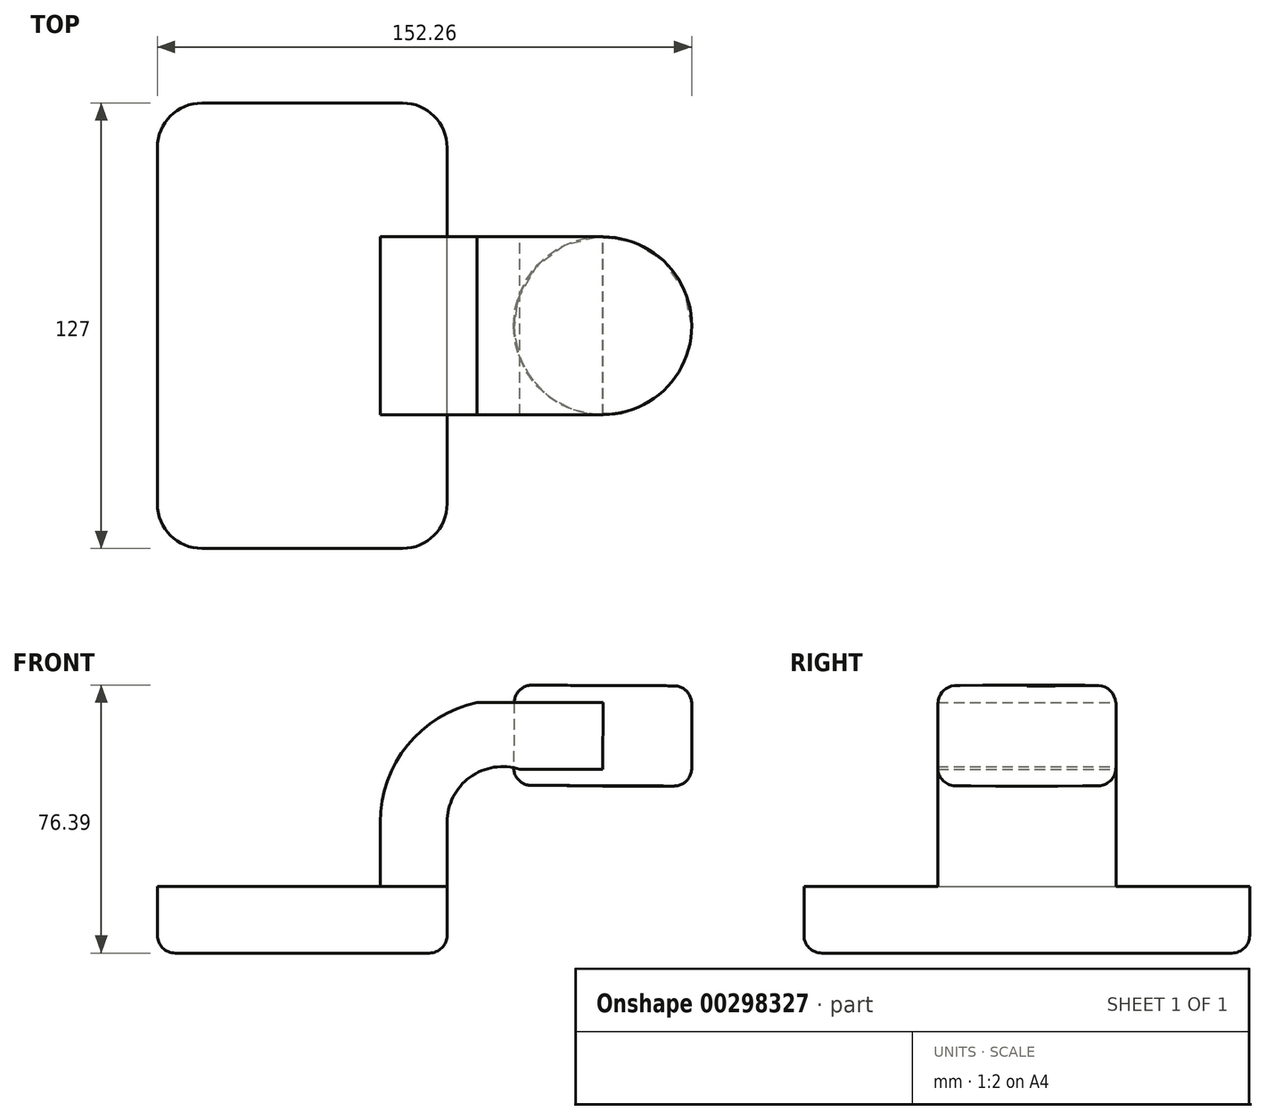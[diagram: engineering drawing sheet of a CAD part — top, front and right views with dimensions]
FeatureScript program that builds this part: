
annotation { "Feature Type Name" : "Feature", "Feature Type Description" : "" }
export const myFeature = defineFeature(function(context is Context, id is Id, definition is map)
    precondition{}
    {
        {
            var Q0;
            Q0=qCreatedBy(makeId("Front.planeOp"),FACE);
            var sketch = newSketch(context, id + "F0", { "sketchPlane" : qUnion([Q0])});
            skLineSegment(sketch, "E0.bottom", {"start": v(-41.27, -9.53) * mm, "end": v(41.28, -9.53) * mm});
            skLineSegment(sketch, "E0.top", {"start": v(-41.28, 9.52) * mm, "end": v(41.28, 9.52) * mm});
            skLineSegment(sketch, "E0.left", {"start": v(-41.28, -9.53) * mm, "end": v(-41.28, 9.52) * mm});
            skLineSegment(sketch, "E0.right", {"start": v(41.28, -9.53) * mm, "end": v(41.28, 9.52) * mm});
            skPoint(sketch, "E0.middle", {"position": v(0, 0) * mm});
            skLineSegment(sketch, "E1.bottom", {"start": v(111, 38.1) * mm, "end": v(60.2, 38.1) * mm});
            skLineSegment(sketch, "E1.top", {"start": v(111, 66.67) * mm, "end": v(60.2, 66.67) * mm});
            skLineSegment(sketch, "E1.left", {"start": v(111, 38.1) * mm, "end": v(111, 66.67) * mm});
            skLineSegment(sketch, "E1.right", {"start": v(60.2, 38.1) * mm, "end": v(60.2, 66.67) * mm});
            skPoint(sketch, "E1.middle", {"position": v(85.6, 52.39) * mm});
            skLineSegment(sketch, "E2", {"start": v(41.28, 9.52) * mm, "end": v(41.28, 27.77) * mm});
            skArc(sketch, "E3", {"start": v(41.28, 27.77) * mm, "mid": v(47.8, 40.6) * mm, "end": v(62.03, 42.88) * mm});
            skLineSegment(sketch, "E4", {"start": v(62.03, 42.88) * mm, "end": v(85.73, 42.88) * mm});
            skLineSegment(sketch, "E5.0", {"start": v(49.86, 61.93) * mm, "end": v(85.73, 61.93) * mm});
            skArc(sketch, "E5.1", {"start": v(22.23, 27.77) * mm, "mid": v(30, 49.74) * mm, "end": v(49.86, 61.93) * mm});
            skLineSegment(sketch, "E5.2", {"start": v(22.22, 9.52) * mm, "end": v(22.22, 27.77) * mm});
            skLineSegment(sketch, "E6", {"start": v(85.6, 38.1) * mm, "end": v(85.73, 66.67) * mm});
            skFitSpline(sketch, "E7", {"points": [v(-41.27, 9.52) * mm, v(49.86, 61.93) * mm], "startDerivative": vector(60.3, 94.1) * mm, "endDerivative": vector(117.08, -0.15) * mm});
            skSolve(sketch);
        }
        {
            var Q0;
            Q0=makeQuery(id+"F0.imprint","IMPRINT",FACE,{"disambiguationData":[TD([[makeQuery(id+"F0.imprint","IMPRINT",EDGE,{"derivedFrom":sQuery(id+"F0.wireOp",EDGE,"E0.bottom")}),1.0]])]});
            extrude(context, id + "F1", {"entities" : qUnion([Q0]), "endBound" : BoundingType.SYMMETRIC, "depth" : 127 * mm});
        }
        {
            var Q0;
            {var subQ1=sQuery(id+"F0.wireOp",EDGE,"E2");Q0=makeQuery(id+"F0.imprint","IMPRINT",FACE,{"disambiguationData":[TD([[makeQuery(id+"F0.imprint","IMPRINT",EDGE,{"derivedFrom":subQ1}),1.0]])]});}
            var Q1;
            {var subQ1=sQuery(id+"F0.wireOp",EDGE,"E1.right");var subQ6=sQuery(id+"F0.wireOp",EDGE,"E3");var subQ8=makeQuery(id+"F0.imprint","INTERSECT",VERTEX,{"derivedFrom":[subQ1,subQ6]});Q1=makeQuery(id+"F0.imprint","IMPRINT",FACE,{"disambiguationData":[TD([[makeQuery(id+"F0.imprint","IMPRINT",EDGE,{"disambiguationData":[TD([[subQ8,-1.0]])],"derivedFrom":subQ1}),-1.0]])]});}
            extrude(context, id + "F2", {"entities" : qUnion([Q0, Q1]), "operationType" : NewBodyOperationType.ADD, "endBound" : BoundingType.SYMMETRIC, "depth" : 50.8 * mm});
        }
        {
            var Q0;
            Q0=makeQuery(id+"F0.imprint","IMPRINT",FACE,{"disambiguationData":[TD([[makeQuery(id+"F0.imprint","IMPRINT",EDGE,{"derivedFrom":sQuery(id+"F0.wireOp",EDGE,"E0.bottom")}),1.0]])]});
            var Q1;
            Q1=makeQuery(id+"F0.imprint","IMPRINT",FACE,{"disambiguationData":[TD([[makeQuery(id+"F0.imprint","IMPRINT",EDGE,{"derivedFrom":sQuery(id+"F0.wireOp",EDGE,"E5.1")}),1.0]])]});
            var Q2;
            {var subQ1=sQuery(id+"F0.wireOp",EDGE,"E2");Q2=makeQuery(id+"F0.imprint","IMPRINT",FACE,{"disambiguationData":[TD([[makeQuery(id+"F0.imprint","IMPRINT",EDGE,{"derivedFrom":subQ1}),1.0]])]});}
            var Q3;
            {var subQ1=sQuery(id+"F0.wireOp",EDGE,"E1.right");var subQ6=sQuery(id+"F0.wireOp",EDGE,"E3");var subQ8=makeQuery(id+"F0.imprint","INTERSECT",VERTEX,{"derivedFrom":[subQ1,subQ6]});Q3=makeQuery(id+"F0.imprint","IMPRINT",FACE,{"disambiguationData":[TD([[makeQuery(id+"F0.imprint","IMPRINT",EDGE,{"disambiguationData":[TD([[subQ8,-1.0]])],"derivedFrom":subQ1}),-1.0]])]});}
            extrude(context, id + "F3", {"entities" : qUnion([Q0, Q1, Q2, Q3]), "operationType" : NewBodyOperationType.ADD, "endBound" : BoundingType.SYMMETRIC, "depth" : 15.88 * mm});
        }
        {
            var Q0;
            {var subQ4=sQuery(id+"F0.wireOp",EDGE,"E1.left");Q0=makeQuery(id+"F0.imprint","IMPRINT",FACE,{"disambiguationData":[TD([[makeQuery(id+"F0.imprint","IMPRINT",EDGE,{"derivedFrom":subQ4}),1.0]])]});}
            var Q1;
            Q1=sQuery(id+"F0.wireOp",EDGE,"E6");
            revolve(context, id + "F4", {"entities" : qUnion([Q0]), "axis" : qUnion([Q1]), "revolveType" : RevolveType.FULL});
        }
        {
            var Q0;
            Q0=makeQuery(id+"F1.opExtrude","CAP_EDGE",EDGE,{"disambiguationData":[OSD([sQuery(id+"F0.wireOp",EDGE,"E0.left")])],"isStart":false});
            var Q1;
            Q1=makeQuery(id+"F1.opExtrude","CAP_EDGE",EDGE,{"disambiguationData":[OSD([sQuery(id+"F0.wireOp",EDGE,"E0.right")])],"isStart":false});
            var Q2;
            Q2=makeQuery(id+"F1.opExtrude","CAP_EDGE",EDGE,{"disambiguationData":[OSD([sQuery(id+"F0.wireOp",EDGE,"E0.right")])],"isStart":true});
            var Q3;
            Q3=makeQuery(id+"F1.opExtrude","CAP_EDGE",EDGE,{"disambiguationData":[OSD([sQuery(id+"F0.wireOp",EDGE,"E0.left")])],"isStart":true});
            fillet(context, id + "F5", {"entities" : qUnion([Q0, Q1, Q2, Q3]), "radius" : 12.7 * mm, "tangentPropagation" : true, "allowEdgeOverflow" : false});
        }
        {
            var Q0;
            Q0=makeQuery(id+"F4.opRevolve","SWEPT_EDGE",EDGE,{"disambiguationData":[OSD([sQuery(id+"F0.wireOp",EDGE,"E1.top"),sQuery(id+"F0.wireOp",EDGE,"E1.left")])]});
            var Q1;
            Q1=makeQuery(id+"F4.opRevolve","SWEPT_EDGE",EDGE,{"disambiguationData":[OSD([sQuery(id+"F0.wireOp",EDGE,"E1.bottom"),sQuery(id+"F0.wireOp",EDGE,"E1.left")])]});
            fillet(context, id + "F6", {"entities" : qUnion([Q0, Q1]), "radius" : 5.08 * mm, "tangentPropagation" : true, "allowEdgeOverflow" : false});
        }
        {
            var Q0;
            Q0=makeQuery(id+"F1.opExtrude","SWEPT_FACE",FACE,{"disambiguationData":[OSD([sQuery(id+"F0.wireOp",EDGE,"E0.bottom")])]});
            fillet(context, id + "F7", {"entities" : qUnion([Q0]), "radius" : 5.08 * mm, "tangentPropagation" : true, "allowEdgeOverflow" : false});
        }
    });
